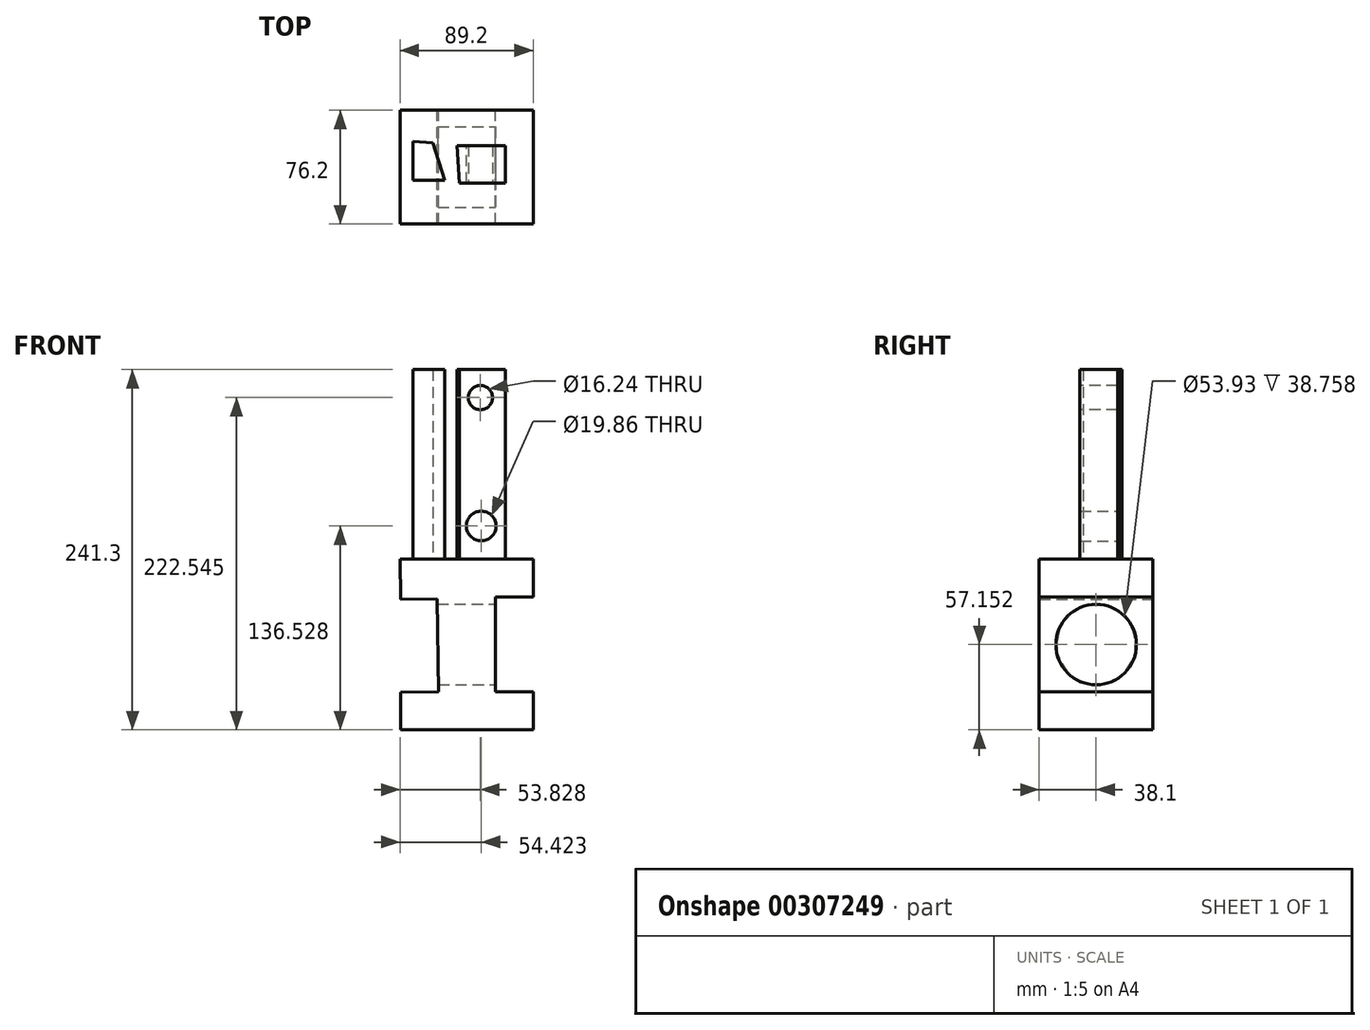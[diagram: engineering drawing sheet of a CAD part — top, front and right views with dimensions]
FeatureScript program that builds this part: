
annotation { "Feature Type Name" : "Feature", "Feature Type Description" : "" }
export const myFeature = defineFeature(function(context is Context, id is Id, definition is map)
    precondition{}
    {
        {
            var Q0;
            Q0=qCreatedBy(makeId("Front.planeOp"),FACE);
            var sketch = newSketch(context, id + "F0", { "sketchPlane" : qUnion([Q0])});
            skLineSegment(sketch, "E0", {"start": v(-32.1, -51.58) * mm, "end": v(56.8, -51.58) * mm});
            skLineSegment(sketch, "E1", {"start": v(56.8, -51.58) * mm, "end": v(56.8, -26.18) * mm});
            skLineSegment(sketch, "E2", {"start": v(56.8, -26.18) * mm, "end": v(31.4, -26.18) * mm});
            skLineSegment(sketch, "E3", {"start": v(31.4, -26.18) * mm, "end": v(31.4, 37.32) * mm});
            skLineSegment(sketch, "E4", {"start": v(31.4, 37.32) * mm, "end": v(56.8, 37.32) * mm});
            skLineSegment(sketch, "E5", {"start": v(56.8, 37.32) * mm, "end": v(56.8, 62.72) * mm});
            skLineSegment(sketch, "E6", {"start": v(56.8, 62.72) * mm, "end": v(-32.39, 62.72) * mm});
            skLineSegment(sketch, "E7", {"start": v(-32.39, 62.72) * mm, "end": v(-32.1, 35.91) * mm});
            skLineSegment(sketch, "E8", {"start": v(-32.1, 35.91) * mm, "end": v(-7.39, 36.19) * mm});
            skLineSegment(sketch, "E9", {"start": v(-7.39, 36.19) * mm, "end": v(-6.7, -26.18) * mm});
            skLineSegment(sketch, "E10", {"start": v(-6.7, -26.18) * mm, "end": v(-32.1, -26.46) * mm});
            skLineSegment(sketch, "E11", {"start": v(-32.1, -26.46) * mm, "end": v(-32.1, -51.58) * mm});
            skSolve(sketch);
        }
        {
            var Q0;
            Q0=makeQuery(id+"F0.imprint","IMPRINT",FACE,{"disambiguationData":[TD([[makeQuery(id+"F0.imprint","IMPRINT",EDGE,{"derivedFrom":sQuery(id+"F0.wireOp",EDGE,"E0")}),1.0]])]});
            extrude(context, id + "F1", {"entities" : qUnion([Q0]), "depth" : 76.2 * mm});
        }
        {
            var Q0;
            Q0=makeQuery(id+"F1.opExtrude","SWEPT_FACE",FACE,{"disambiguationData":[OSD([sQuery(id+"F0.wireOp",EDGE,"E3")])]});
            var sketch = newSketch(context, id + "F2", { "sketchPlane" : qUnion([Q0])});
            skCircle(sketch, "E12", {"center": v(-38.1, 5.57) * mm, "radius": 26.96 * mm});
            skPoint(sketch, "E12.centerSnap0", {"position": v(-38.1, 37.32) * mm});
            skPoint(sketch, "E12.centerSnap1", {"position": v(-76.2, 5.57) * mm});
            skSolve(sketch);
        }
        {
            var Q0;
            Q0=makeQuery(id+"F2.imprint","IMPRINT",FACE,{"disambiguationData":[TD([[makeQuery(id+"F2.imprint","IMPRINT",EDGE,{"derivedFrom":sQuery(id+"F2.wireOp",EDGE,"E12")}),1.0]])]});
            extrude(context, id + "F3", {"entities" : qUnion([Q0]), "operationType" : NewBodyOperationType.REMOVE, "endBound" : BoundingType.THROUGH_ALL, "oppositeDirection" : true, "depth" : 25.4 * mm});
        }
        {
            var Q0;
            Q0=makeQuery(id+"F1.opExtrude","SWEPT_FACE",FACE,{"disambiguationData":[OSD([sQuery(id+"F0.wireOp",EDGE,"E6")])]});
            var sketch = newSketch(context, id + "F4", { "sketchPlane" : qUnion([Q0])});
            skLineSegment(sketch, "E13", {"start": v(7.3, -48.92) * mm, "end": v(38.35, -48.92) * mm});
            skLineSegment(sketch, "E14", {"start": v(38.35, -48.92) * mm, "end": v(38.35, -23.6) * mm});
            skLineSegment(sketch, "E15", {"start": v(38.35, -23.6) * mm, "end": v(5.72, -23.6) * mm});
            skLineSegment(sketch, "E16", {"start": v(5.72, -23.6) * mm, "end": v(7.3, -48.92) * mm});
            skSolve(sketch);
        }
        {
            var Q0;
            Q0=makeQuery(id+"F4.imprint","IMPRINT",FACE,{"disambiguationData":[TD([[makeQuery(id+"F4.imprint","IMPRINT",EDGE,{"derivedFrom":sQuery(id+"F4.wireOp",EDGE,"E13")}),1.0]])]});
            extrude(context, id + "F5", {"entities" : qUnion([Q0]), "operationType" : NewBodyOperationType.ADD, "depth" : 127 * mm});
        }
        {
            var Q0;
            Q0=makeQuery(id+"F1.opExtrude","SWEPT_FACE",FACE,{"disambiguationData":[OSD([sQuery(id+"F0.wireOp",EDGE,"E6")])]});
            var sketch = newSketch(context, id + "F6", { "sketchPlane" : qUnion([Q0])});
            skLineSegment(sketch, "E17", {"start": v(-10.3, -21.7) * mm, "end": v(-2.5, -46.94) * mm});
            skLineSegment(sketch, "E18", {"start": v(-2.5, -46.94) * mm, "end": v(-23.88, -46.94) * mm});
            skLineSegment(sketch, "E19", {"start": v(-23.88, -46.94) * mm, "end": v(-23.88, -20.91) * mm});
            skLineSegment(sketch, "E20", {"start": v(-23.88, -20.91) * mm, "end": v(-10.3, -21.7) * mm});
            skSolve(sketch);
        }
        {
            var Q0;
            Q0=makeQuery(id+"F6.imprint","IMPRINT",FACE,{"disambiguationData":[TD([[makeQuery(id+"F6.imprint","IMPRINT",EDGE,{"derivedFrom":sQuery(id+"F6.wireOp",EDGE,"E17")}),-1.0]])]});
            extrude(context, id + "F7", {"entities" : qUnion([Q0]), "operationType" : NewBodyOperationType.ADD, "depth" : 127 * mm});
        }
        {
            var Q0;
            Q0=makeQuery(id+"F5.opExtrude","SWEPT_FACE",FACE,{"disambiguationData":[OSD([sQuery(id+"F4.wireOp",EDGE,"E13")])]});
            var sketch = newSketch(context, id + "F8", { "sketchPlane" : qUnion([Q0])});
            skCircle(sketch, "E21", {"center": v(21.44, 170.97) * mm, "radius": 8.12 * mm});
            skSolve(sketch);
        }
        {
            var Q0;
            Q0=makeQuery(id+"F8.imprint","IMPRINT",FACE,{"disambiguationData":[TD([[makeQuery(id+"F8.imprint","IMPRINT",EDGE,{"derivedFrom":sQuery(id+"F8.wireOp",EDGE,"E21")}),1.0]])]});
            extrude(context, id + "F9", {"entities" : qUnion([Q0]), "operationType" : NewBodyOperationType.REMOVE, "endBound" : BoundingType.THROUGH_ALL, "oppositeDirection" : true, "depth" : 25.4 * mm});
        }
        {
            var Q0;
            Q0=makeQuery(id+"F5.opExtrude","SWEPT_FACE",FACE,{"disambiguationData":[OSD([sQuery(id+"F4.wireOp",EDGE,"E15")])]});
            var sketch = newSketch(context, id + "F10", { "sketchPlane" : qUnion([Q0])});
            skCircle(sketch, "E22", {"center": v(-22.03, 84.95) * mm, "radius": 9.93 * mm});
            skPoint(sketch, "E22.centerSnap0", {"position": v(-22.03, 62.72) * mm});
            skSolve(sketch);
        }
        {
            var Q0;
            Q0=makeQuery(id+"F10.imprint","IMPRINT",FACE,{"disambiguationData":[TD([[makeQuery(id+"F10.imprint","IMPRINT",EDGE,{"derivedFrom":sQuery(id+"F10.wireOp",EDGE,"E22")}),1.0]])]});
            extrude(context, id + "F11", {"entities" : qUnion([Q0]), "operationType" : NewBodyOperationType.REMOVE, "endBound" : BoundingType.THROUGH_ALL, "oppositeDirection" : true, "depth" : 25.4 * mm});
        }
    });
